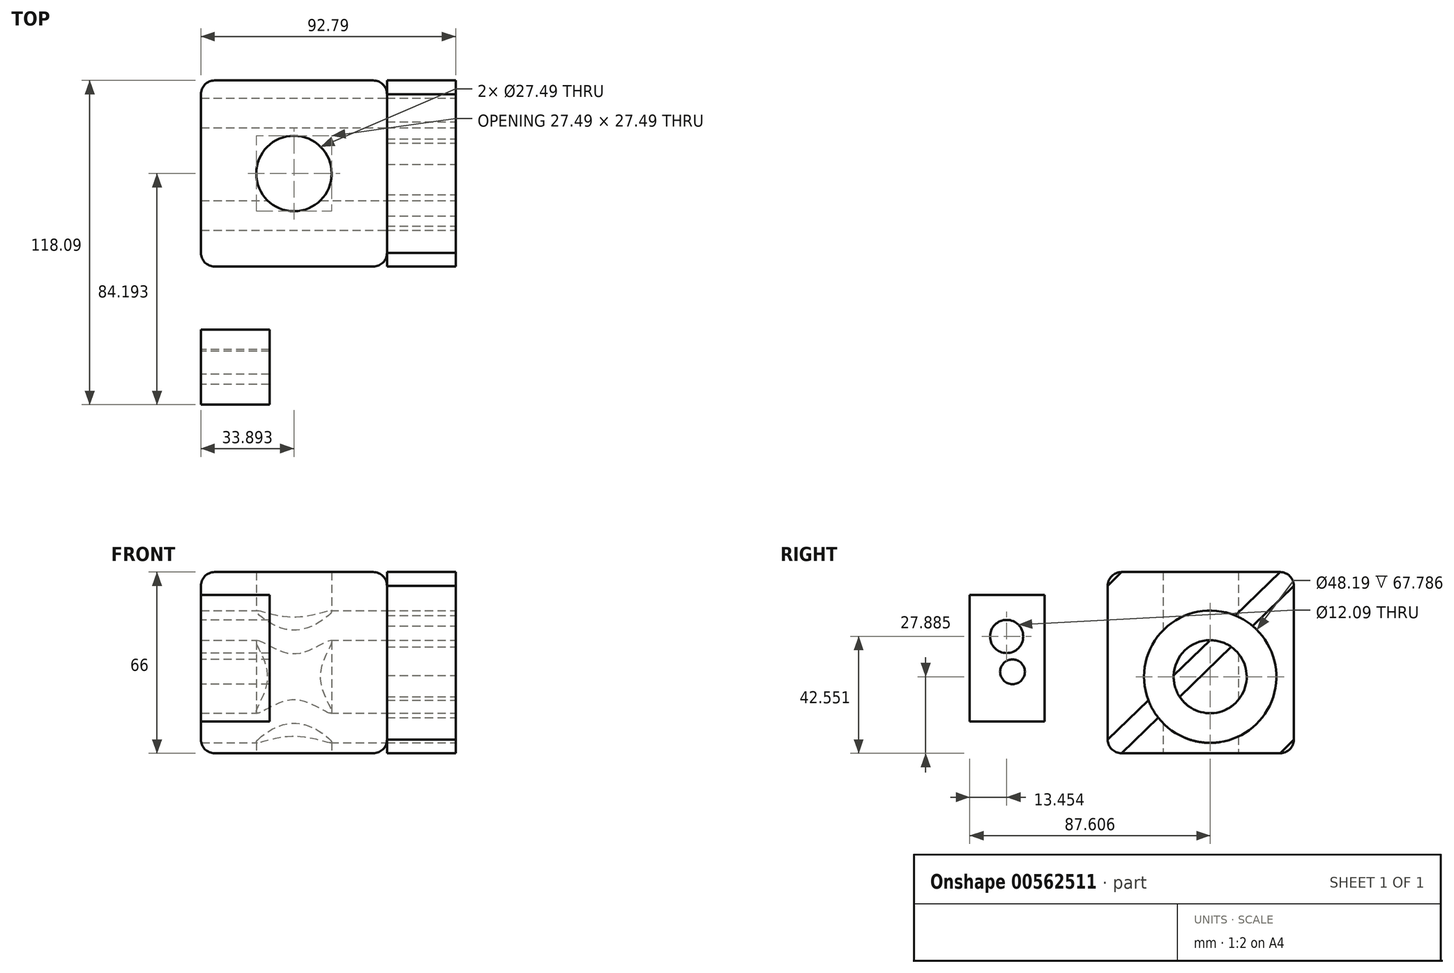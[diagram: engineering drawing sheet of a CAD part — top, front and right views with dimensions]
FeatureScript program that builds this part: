
annotation { "Feature Type Name" : "Feature", "Feature Type Description" : "" }
export const myFeature = defineFeature(function(context is Context, id is Id, definition is map)
    precondition{}
    {
        {
            var Q0;
            Q0=qCreatedBy(makeId("Top.planeOp"),FACE);
            var sketch = newSketch(context, id + "F0", { "sketchPlane" : qUnion([Q0])});
            skLineSegment(sketch, "E0.bottom", {"start": v(0, 0) * mm, "end": v(67.79, 0) * mm});
            skLineSegment(sketch, "E0.top", {"start": v(0, 67.79) * mm, "end": v(67.79, 67.79) * mm});
            skLineSegment(sketch, "E0.left", {"start": v(0, 0) * mm, "end": v(0, 67.79) * mm});
            skLineSegment(sketch, "E0.right", {"start": v(67.79, 0) * mm, "end": v(67.79, 67.79) * mm});
            skCircle(sketch, "E1", {"center": v(33.9, 33.9) * mm, "radius": 13.74 * mm});
            skLineSegment(sketch, "E2", {"start": v(0, 33.9) * mm, "end": v(67.79, 33.9) * mm, "construction": true});
            skSolve(sketch);
        }
        {
            var Q0;
            Q0 = qSketchRegion(id + "F0", true);
            extrude(context, id + "F1", {"entities" : qUnion([Q0]), "depth" : 66 * mm, "offsetDistance" : 25 * mm});
        }
        {
            var Q0;
            Q0=makeQuery(id+"F1.opExtrude","CAP_EDGE",EDGE,{"disambiguationData":[OSD([sQuery(id+"F0.wireOp",EDGE,"E0.left")])],"isStart":false});
            var Q1;
            Q1=makeQuery(id+"F1.opExtrude","CAP_EDGE",EDGE,{"disambiguationData":[OSD([sQuery(id+"F0.wireOp",EDGE,"E0.bottom")])],"isStart":false});
            var Q2;
            Q2=makeQuery(id+"F1.opExtrude","CAP_EDGE",EDGE,{"disambiguationData":[OSD([sQuery(id+"F0.wireOp",EDGE,"E0.right")])],"isStart":false});
            var Q3;
            Q3=makeQuery(id+"F1.opExtrude","CAP_EDGE",EDGE,{"disambiguationData":[OSD([sQuery(id+"F0.wireOp",EDGE,"E0.top")])],"isStart":false});
            var Q4;
            Q4=makeQuery(id+"F1.opExtrude","SWEPT_EDGE",EDGE,{"disambiguationData":[OSD([sQuery(id+"F0.wireOp",EDGE,"E0.top"),sQuery(id+"F0.wireOp",EDGE,"E0.right")])]});
            var Q5;
            Q5=makeQuery(id+"F1.opExtrude","SWEPT_EDGE",EDGE,{"disambiguationData":[OSD([sQuery(id+"F0.wireOp",EDGE,"E0.bottom"),sQuery(id+"F0.wireOp",EDGE,"E0.right")])]});
            var Q6;
            Q6=makeQuery(id+"F1.opExtrude","SWEPT_EDGE",EDGE,{"disambiguationData":[OSD([sQuery(id+"F0.wireOp",EDGE,"E0.bottom"),sQuery(id+"F0.wireOp",EDGE,"E0.left")])]});
            var Q7;
            Q7=makeQuery(id+"F1.opExtrude","SWEPT_EDGE",EDGE,{"disambiguationData":[OSD([sQuery(id+"F0.wireOp",EDGE,"E0.top"),sQuery(id+"F0.wireOp",EDGE,"E0.left")])]});
            var Q8;
            Q8=makeQuery(id+"F1.opExtrude","CAP_EDGE",EDGE,{"disambiguationData":[OSD([sQuery(id+"F0.wireOp",EDGE,"E0.top")])],"isStart":true});
            var Q9;
            Q9=makeQuery(id+"F1.opExtrude","CAP_EDGE",EDGE,{"disambiguationData":[OSD([sQuery(id+"F0.wireOp",EDGE,"E0.left")])],"isStart":true});
            var Q10;
            Q10=makeQuery(id+"F1.opExtrude","CAP_EDGE",EDGE,{"disambiguationData":[OSD([sQuery(id+"F0.wireOp",EDGE,"E0.bottom")])],"isStart":true});
            var Q11;
            Q11=makeQuery(id+"F1.opExtrude","CAP_EDGE",EDGE,{"disambiguationData":[OSD([sQuery(id+"F0.wireOp",EDGE,"E0.right")])],"isStart":true});
            fillet(context, id + "F2", {"entities" : qUnion([Q0, Q1, Q2, Q3, Q4, Q5, Q6, Q7, Q8, Q9, Q10, Q11]), "radius" : 5 * mm, "tangentPropagation" : true, "allowEdgeOverflow" : false});
        }
        {
            var Q0;
            Q0=makeQuery(id+"F1.opExtrude","SWEPT_FACE",FACE,{"disambiguationData":[OSD([sQuery(id+"F0.wireOp",EDGE,"E0.right")])]});
            var sketch = newSketch(context, id + "F3", { "sketchPlane" : qUnion([Q0])});
            skLineSegment(sketch, "E3.0", {"start": v(67.79, 61) * mm, "end": v(67.79, 5) * mm});
            skLineSegment(sketch, "E3.1", {"start": v(62.79, 0) * mm, "end": v(5, 0) * mm});
            skLineSegment(sketch, "E3.2", {"start": v(5, 66) * mm, "end": v(62.79, 66) * mm});
            skLineSegment(sketch, "E3.3", {"start": v(0, 5) * mm, "end": v(0, 61) * mm});
            skLineSegment(sketch, "E4", {"start": v(5, 0) * mm, "end": v(67.79, 61) * mm});
            skLineSegment(sketch, "E5", {"start": v(0, 5) * mm, "end": v(62.79, 66) * mm});
            skLineSegment(sketch, "E6", {"start": v(0, 61) * mm, "end": v(5, 66) * mm});
            skLineSegment(sketch, "E7", {"start": v(62.79, 0) * mm, "end": v(67.79, 5) * mm});
            skSolve(sketch);
        }
        {
            var Q0;
            Q0 = qSketchRegion(id + "F3", true);
            extrude(context, id + "F4", {"entities" : qUnion([Q0]), "depth" : 25 * mm, "offsetDistance" : 25 * mm});
        }
        {
            var Q0;
            Q0=makeQuery(id+"F1.opExtrude","SWEPT_FACE",FACE,{"disambiguationData":[OSD([sQuery(id+"F0.wireOp",EDGE,"E0.left")])]});
            var sketch = newSketch(context, id + "F5", { "sketchPlane" : qUnion([Q0])});
            skCircle(sketch, "E8", {"center": v(-37.3, 27.88) * mm, "radius": 13.3 * mm});
            skCircle(sketch, "E9", {"center": v(-37.3, 27.88) * mm, "radius": 24.1 * mm});
            skSolve(sketch);
        }
        {
            var Q0;
            Q0 = qSketchRegion(id + "F5", true);
            var Q1;
            Q1=makeQuery(id+"F4.opExtrude","CAP_FACE",FACE,{"disambiguationData":[OSD([sQuery(id+"F3.wireOp",EDGE,"E3.2"),sQuery(id+"F3.wireOp",EDGE,"E3.3"),sQuery(id+"F3.wireOp",EDGE,"E5"),sQuery(id+"F3.wireOp",EDGE,"E6")])],"isStart":false});
            extrude(context, id + "F6", {"entities" : qUnion([Q0]), "depth" : 25 * mm, "offsetDistance" : 25 * mm, "hasSecondDirection" : true, "secondDirectionBound" : SecondDirectionBoundingType.UP_TO_SURFACE, "secondDirectionOppositeDirection" : true, "secondDirectionDepth" : 25 * mm, "secondDirectionBoundEntityFace" : qUnion([Q1])});
        }
        {
            var Q0;
            Q0=makeQuery(id+"F6.opExtrude","SWEPT_BODY",BODY,{"disambiguationData":[OSD([sQuery(id+"F5.wireOp",EDGE,"E8"),sQuery(id+"F5.wireOp",EDGE,"E9")])]});
            var Q1;
            Q1=makeQuery(id+"F4.opExtrude","SWEPT_BODY",BODY,{"disambiguationData":[OSD([sQuery(id+"F3.wireOp",EDGE,"E3.2"),sQuery(id+"F3.wireOp",EDGE,"E3.3"),sQuery(id+"F3.wireOp",EDGE,"E5"),sQuery(id+"F3.wireOp",EDGE,"E6")])]});
            var Q2;
            Q2=makeQuery(id+"F4.opExtrude","SWEPT_BODY",BODY,{"disambiguationData":[OSD([sQuery(id+"F3.wireOp",EDGE,"E3.0"),sQuery(id+"F3.wireOp",EDGE,"E3.1"),sQuery(id+"F3.wireOp",EDGE,"E4"),sQuery(id+"F3.wireOp",EDGE,"E7")])]});
            var Q3;
            Q3=makeQuery(id+"F1.opExtrude","SWEPT_BODY",BODY,{"disambiguationData":[OSD([sQuery(id+"F0.wireOp",EDGE,"E0.bottom"),sQuery(id+"F0.wireOp",EDGE,"E0.top"),sQuery(id+"F0.wireOp",EDGE,"E0.left"),sQuery(id+"F0.wireOp",EDGE,"E0.right"),sQuery(id+"F0.wireOp",EDGE,"E1")])]});
            booleanBodies(context, id + "F7", {"operationType" : BooleanOperationType.SUBTRACTION, "tools" : qUnion([Q0]), "targets" : qUnion([Q1, Q2, Q3])});
        }
        {
            var Q0;
            Q0=qCreatedBy(makeId("Right.planeOp"),FACE);
            var sketch = newSketch(context, id + "F8", { "sketchPlane" : qUnion([Q0])});
            skLineSegment(sketch, "E10.bottom", {"start": v(-50.3, 57.66) * mm, "end": v(-22.98, 57.66) * mm});
            skLineSegment(sketch, "E10.top", {"start": v(-50.3, 11.54) * mm, "end": v(-22.98, 11.54) * mm});
            skLineSegment(sketch, "E10.left", {"start": v(-50.3, 57.66) * mm, "end": v(-50.3, 11.54) * mm});
            skLineSegment(sketch, "E10.right", {"start": v(-22.98, 57.66) * mm, "end": v(-22.98, 11.54) * mm});
            skCircle(sketch, "E11", {"center": v(-36.85, 42.55) * mm, "radius": 6.04 * mm});
            skCircle(sketch, "E12", {"center": v(-34.7, 29.68) * mm, "radius": 4.52 * mm});
            skSolve(sketch);
        }
        {
            var Q0;
            Q0 = qSketchRegion(id + "F8", true);
            extrude(context, id + "F9", {"entities" : qUnion([Q0]), "depth" : 25 * mm, "offsetDistance" : 25 * mm});
        }
    });
